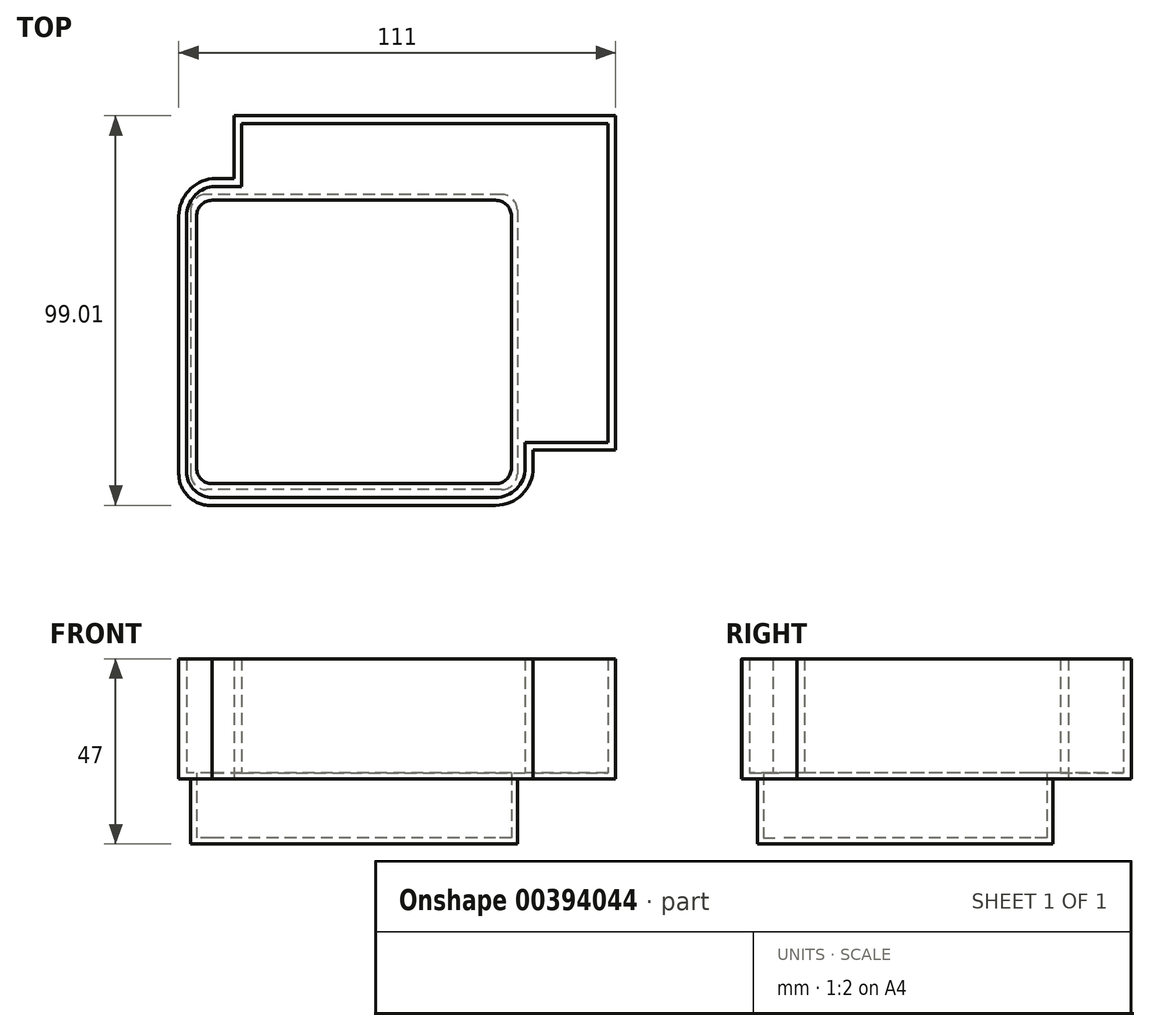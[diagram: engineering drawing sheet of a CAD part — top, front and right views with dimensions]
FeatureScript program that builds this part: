
annotation { "Feature Type Name" : "Feature", "Feature Type Description" : "" }
export const myFeature = defineFeature(function(context is Context, id is Id, definition is map)
    precondition{}
    {
        {
            var Q0;
            Q0=qCreatedBy(makeId("Top.planeOp"),FACE);
            var sketch = newSketch(context, id + "F0", { "sketchPlane" : qUnion([Q0])});
            skLineSegment(sketch, "E0.bottom", {"start": v(37.5, 37.5) * mm, "end": v(-37.5, 37.5) * mm});
            skLineSegment(sketch, "E0.top", {"start": v(37.5, -37.5) * mm, "end": v(-37.5, -37.5) * mm});
            skLineSegment(sketch, "E0.left", {"start": v(41.5, 33.5) * mm, "end": v(41.5, -33.5) * mm});
            skLineSegment(sketch, "E0.right", {"start": v(-41.5, 33.5) * mm, "end": v(-41.5, -33.5) * mm});
            skPoint(sketch, "E0.middle", {"position": v(0, 0) * mm});
            skPoint(sketch, "E1", {"position": v(-37.5, 37.5) * mm});
            skPoint(sketch, "E2", {"position": v(-41.5, 33.5) * mm});
            skArc(sketch, "E3", {"start": v(-37.5, 37.5) * mm, "mid": v(-40.33, 36.33) * mm, "end": v(-41.5, 33.5) * mm});
            skPoint(sketch, "E4.orphan", {"position": v(-41.5, 37.5) * mm});
            skArc(sketch, "E5.MirrorCS", {"start": v(37.5, 37.5) * mm, "mid": v(40.33, 36.33) * mm, "end": v(41.5, 33.5) * mm});
            skPoint(sketch, "E6.orphan", {"position": v(41.5, 37.5) * mm});
            skArc(sketch, "E7.MirrorCS", {"start": v(-37.5, -37.5) * mm, "mid": v(-40.33, -36.33) * mm, "end": v(-41.5, -33.5) * mm});
            skArc(sketch, "E8.MirrorCS", {"start": v(37.5, -37.5) * mm, "mid": v(40.33, -36.33) * mm, "end": v(41.5, -33.5) * mm});
            skPoint(sketch, "E9.orphan", {"position": v(-41.5, -37.5) * mm});
            skPoint(sketch, "E10.orphan", {"position": v(41.5, -37.5) * mm});
            skSolve(sketch);
        }
        {
            var Q0;
            Q0=makeQuery(id+"F0.imprint","IMPRINT",FACE,{"disambiguationData":[TD([[makeQuery(id+"F0.imprint","IMPRINT",EDGE,{"derivedFrom":sQuery(id+"F0.wireOp",EDGE,"E0.bottom")}),1.0]])]});
            extrude(context, id + "F1", {"entities" : qUnion([Q0]), "depth" : 1.5 * mm});
        }
        {
            var Q0;
            Q0=makeQuery(id+"F1.opExtrude","CAP_FACE",FACE,{"disambiguationData":[OSD([sQuery(id+"F0.wireOp",EDGE,"E0.bottom"),sQuery(id+"F0.wireOp",EDGE,"E0.top"),sQuery(id+"F0.wireOp",EDGE,"E0.left"),sQuery(id+"F0.wireOp",EDGE,"E0.right"),sQuery(id+"F0.wireOp",EDGE,"E3"),sQuery(id+"F0.wireOp",EDGE,"E5.MirrorCS"),sQuery(id+"F0.wireOp",EDGE,"E7.MirrorCS"),sQuery(id+"F0.wireOp",EDGE,"E8.MirrorCS")])],"isStart":false});
            var sketch = newSketch(context, id + "F2", { "sketchPlane" : qUnion([Q0])});
            skLineSegment(sketch, "E11.bottom", {"start": v(36, 36) * mm, "end": v(-36, 36) * mm});
            skLineSegment(sketch, "E11.top", {"start": v(36, -36) * mm, "end": v(-36, -36) * mm});
            skLineSegment(sketch, "E11.left", {"start": v(40, 32) * mm, "end": v(40, -32) * mm});
            skLineSegment(sketch, "E11.right", {"start": v(-40, 32) * mm, "end": v(-40, -32) * mm});
            skPoint(sketch, "E11.middle", {"position": v(0, 0) * mm});
            skPoint(sketch, "E12", {"position": v(-36, 36) * mm});
            skPoint(sketch, "E13", {"position": v(-40, 32) * mm});
            skArc(sketch, "E14", {"start": v(-36, 36) * mm, "mid": v(-38.83, 34.83) * mm, "end": v(-40, 32) * mm});
            skPoint(sketch, "E15.orphan", {"position": v(-40, 36) * mm});
            skArc(sketch, "E16.MirrorCS", {"start": v(36, 36) * mm, "mid": v(38.83, 34.83) * mm, "end": v(40, 32) * mm});
            skPoint(sketch, "E17.orphan", {"position": v(40, 36) * mm});
            skArc(sketch, "E18.MirrorCS", {"start": v(-36, -36) * mm, "mid": v(-38.83, -34.83) * mm, "end": v(-40, -32) * mm});
            skArc(sketch, "E19.MirrorCS", {"start": v(36, -36) * mm, "mid": v(38.83, -34.83) * mm, "end": v(40, -32) * mm});
            skPoint(sketch, "E20.orphan", {"position": v(-40, -36) * mm});
            skPoint(sketch, "E21.orphan", {"position": v(40, -36) * mm});
            skSolve(sketch);
        }
        {
            var Q0;
            Q0=makeQuery(id+"F2.imprint","IMPRINT",FACE,{"disambiguationData":[TD([[makeQuery(id+"F2.imprint","IMPRINT",EDGE,{"derivedFrom":sQuery(id+"F2.wireOp",EDGE,"E11.bottom")}),-1.0]])]});
            extrude(context, id + "F3", {"entities" : qUnion([Q0]), "operationType" : NewBodyOperationType.ADD, "depth" : 15 * mm});
        }
        {
            var Q0;
            Q0=makeQuery(id+"F3.opExtrude","CAP_FACE",FACE,{"disambiguationData":[OSD([sQuery(id+"F0.wireOp",EDGE,"E0.bottom"),sQuery(id+"F0.wireOp",EDGE,"E0.top"),sQuery(id+"F0.wireOp",EDGE,"E0.left"),sQuery(id+"F0.wireOp",EDGE,"E0.right"),sQuery(id+"F0.wireOp",EDGE,"E3"),sQuery(id+"F0.wireOp",EDGE,"E5.MirrorCS"),sQuery(id+"F0.wireOp",EDGE,"E7.MirrorCS"),sQuery(id+"F0.wireOp",EDGE,"E8.MirrorCS"),sQuery(id+"F2.wireOp",EDGE,"E11.bottom"),sQuery(id+"F2.wireOp",EDGE,"E11.top"),sQuery(id+"F2.wireOp",EDGE,"E11.left"),sQuery(id+"F2.wireOp",EDGE,"E11.right"),sQuery(id+"F2.wireOp",EDGE,"E14"),sQuery(id+"F2.wireOp",EDGE,"E16.MirrorCS"),sQuery(id+"F2.wireOp",EDGE,"E18.MirrorCS"),sQuery(id+"F2.wireOp",EDGE,"E19.MirrorCS")])],"isStart":false});
            var sketch = newSketch(context, id + "F4", { "sketchPlane" : qUnion([Q0])});
            skLineSegment(sketch, "E22", {"start": v(45.5, -27.5) * mm, "end": v(66.5, -27.5) * mm});
            skLineSegment(sketch, "E23", {"start": v(66.5, -27.5) * mm, "end": v(66.5, 57.5) * mm});
            skLineSegment(sketch, "E24", {"start": v(66.5, 57.5) * mm, "end": v(-30.5, 57.5) * mm});
            skLineSegment(sketch, "E25", {"start": v(-30.5, 57.5) * mm, "end": v(-30.5, 41.5) * mm});
            skLineSegment(sketch, "E26", {"start": v(-36, -41.5) * mm, "end": v(36, -41.5) * mm});
            skLineSegment(sketch, "E27", {"start": v(45.5, -27.5) * mm, "end": v(45.5, -32) * mm});
            skArc(sketch, "E28", {"start": v(36, -41.5) * mm, "mid": v(42.72, -38.72) * mm, "end": v(45.5, -32) * mm});
            skLineSegment(sketch, "E29", {"start": v(-44.5, 32) * mm, "end": v(-44.5, -33.5) * mm});
            skArc(sketch, "E30", {"start": v(-44.5, -33.5) * mm, "mid": v(-41.98, -39.34) * mm, "end": v(-36, -41.5) * mm});
            skLineSegment(sketch, "E31", {"start": v(-36, 41.5) * mm, "end": v(-30.5, 41.5) * mm});
            skArc(sketch, "E32", {"start": v(-36, 41.5) * mm, "mid": v(-42.06, 38.37) * mm, "end": v(-44.5, 32) * mm});
            skSolve(sketch);
        }
        {
            var Q0;
            Q0=makeQuery(id+"F4.imprint","IMPRINT",FACE,{"disambiguationData":[TD([[makeQuery(id+"F4.imprint","IMPRINT",EDGE,{"derivedFrom":sQuery(id+"F4.wireOp",EDGE,"E22")}),1.0]])]});
            var Q1;
            Q1=makeQuery(id+"F4.imprint","IMPRINT",FACE,{"disambiguationData":[TD([[makeQuery(id+"F4.imprint","IMPRINT",EDGE,{"derivedFrom":makeQuery(id+"F3.opExtrude","CAP_EDGE",EDGE,{"disambiguationData":[OSD([sQuery(id+"F2.wireOp",EDGE,"E11.bottom")])],"isStart":false})}),-1.0]])]});
            extrude(context, id + "F5", {"entities" : qUnion([Q0, Q1]), "operationType" : NewBodyOperationType.ADD, "depth" : 1.5 * mm});
        }
        {
            var Q0;
            Q0=makeQuery(id+"F5.opExtrude","CAP_FACE",FACE,{"disambiguationData":[OSD([sQuery(id+"F2.wireOp",EDGE,"E11.bottom"),sQuery(id+"F2.wireOp",EDGE,"E11.top"),sQuery(id+"F2.wireOp",EDGE,"E11.left"),sQuery(id+"F2.wireOp",EDGE,"E11.right"),sQuery(id+"F2.wireOp",EDGE,"E14"),sQuery(id+"F2.wireOp",EDGE,"E16.MirrorCS"),sQuery(id+"F2.wireOp",EDGE,"E18.MirrorCS"),sQuery(id+"F2.wireOp",EDGE,"E19.MirrorCS"),sQuery(id+"F4.wireOp",EDGE,"E22"),sQuery(id+"F4.wireOp",EDGE,"E23"),sQuery(id+"F4.wireOp",EDGE,"E24"),sQuery(id+"F4.wireOp",EDGE,"E25"),sQuery(id+"F4.wireOp",EDGE,"E26"),sQuery(id+"F4.wireOp",EDGE,"E27"),sQuery(id+"F4.wireOp",EDGE,"E28"),sQuery(id+"F4.wireOp",EDGE,"E29"),sQuery(id+"F4.wireOp",EDGE,"E30"),sQuery(id+"F4.wireOp",EDGE,"E31"),sQuery(id+"F4.wireOp",EDGE,"E32")])],"isStart":false});
            var sketch = newSketch(context, id + "F6", { "sketchPlane" : qUnion([Q0])});
            skLineSegment(sketch, "E33", {"start": v(-36, 39.5) * mm, "end": v(-28.5, 39.5) * mm});
            skLineSegment(sketch, "E34", {"start": v(-28.5, 39.5) * mm, "end": v(-28.5, 55.5) * mm});
            skLineSegment(sketch, "E35", {"start": v(-28.5, 55.5) * mm, "end": v(64.5, 55.5) * mm});
            skLineSegment(sketch, "E36", {"start": v(64.5, 55.5) * mm, "end": v(64.5, -25.5) * mm});
            skLineSegment(sketch, "E37", {"start": v(64.5, -25.5) * mm, "end": v(43.5, -25.5) * mm});
            skLineSegment(sketch, "E38", {"start": v(43.5, -25.5) * mm, "end": v(43.5, -32) * mm});
            skLineSegment(sketch, "E39", {"start": v(-36, 39.5) * mm, "end": v(-36, 41.5) * mm});
            skLineSegment(sketch, "E40", {"start": v(45.5, -32) * mm, "end": v(43.5, -32) * mm});
            skLineSegment(sketch, "E41", {"start": v(-42.5, 32) * mm, "end": v(-42.5, -33.5) * mm});
            skLineSegment(sketch, "E42", {"start": v(-36, -39.5) * mm, "end": v(36, -39.5) * mm});
            skArc(sketch, "E43", {"start": v(-36, 39.5) * mm, "mid": v(-40.65, 36.96) * mm, "end": v(-42.5, 32) * mm});
            skArc(sketch, "E44", {"start": v(-42.5, -33.5) * mm, "mid": v(-40.42, -37.77) * mm, "end": v(-36, -39.5) * mm});
            skArc(sketch, "E45", {"start": v(36, -39.5) * mm, "mid": v(41.3, -37.3) * mm, "end": v(43.5, -32) * mm});
            skSolve(sketch);
        }
        {
            var Q0;
            Q0=makeQuery(id+"F6.imprint","IMPRINT",FACE,{"disambiguationData":[TD([[makeQuery(id+"F6.imprint","IMPRINT",EDGE,{"derivedFrom":sQuery(id+"F6.wireOp",EDGE,"E33")}),1.0]])]});
            extrude(context, id + "F7", {"entities" : qUnion([Q0]), "operationType" : NewBodyOperationType.ADD, "depth" : 29 * mm});
        }
        {
            var Q0;
            Q0=makeQuery(id+"F6.imprint","IMPRINT",FACE,{"disambiguationData":[TD([[makeQuery(id+"F6.imprint","IMPRINT",EDGE,{"derivedFrom":sQuery(id+"F6.wireOp",EDGE,"E39")}),1.0]])]});
            extrude(context, id + "F8", {"entities" : qUnion([Q0]), "operationType" : NewBodyOperationType.ADD, "depth" : 29 * mm});
        }
    });
